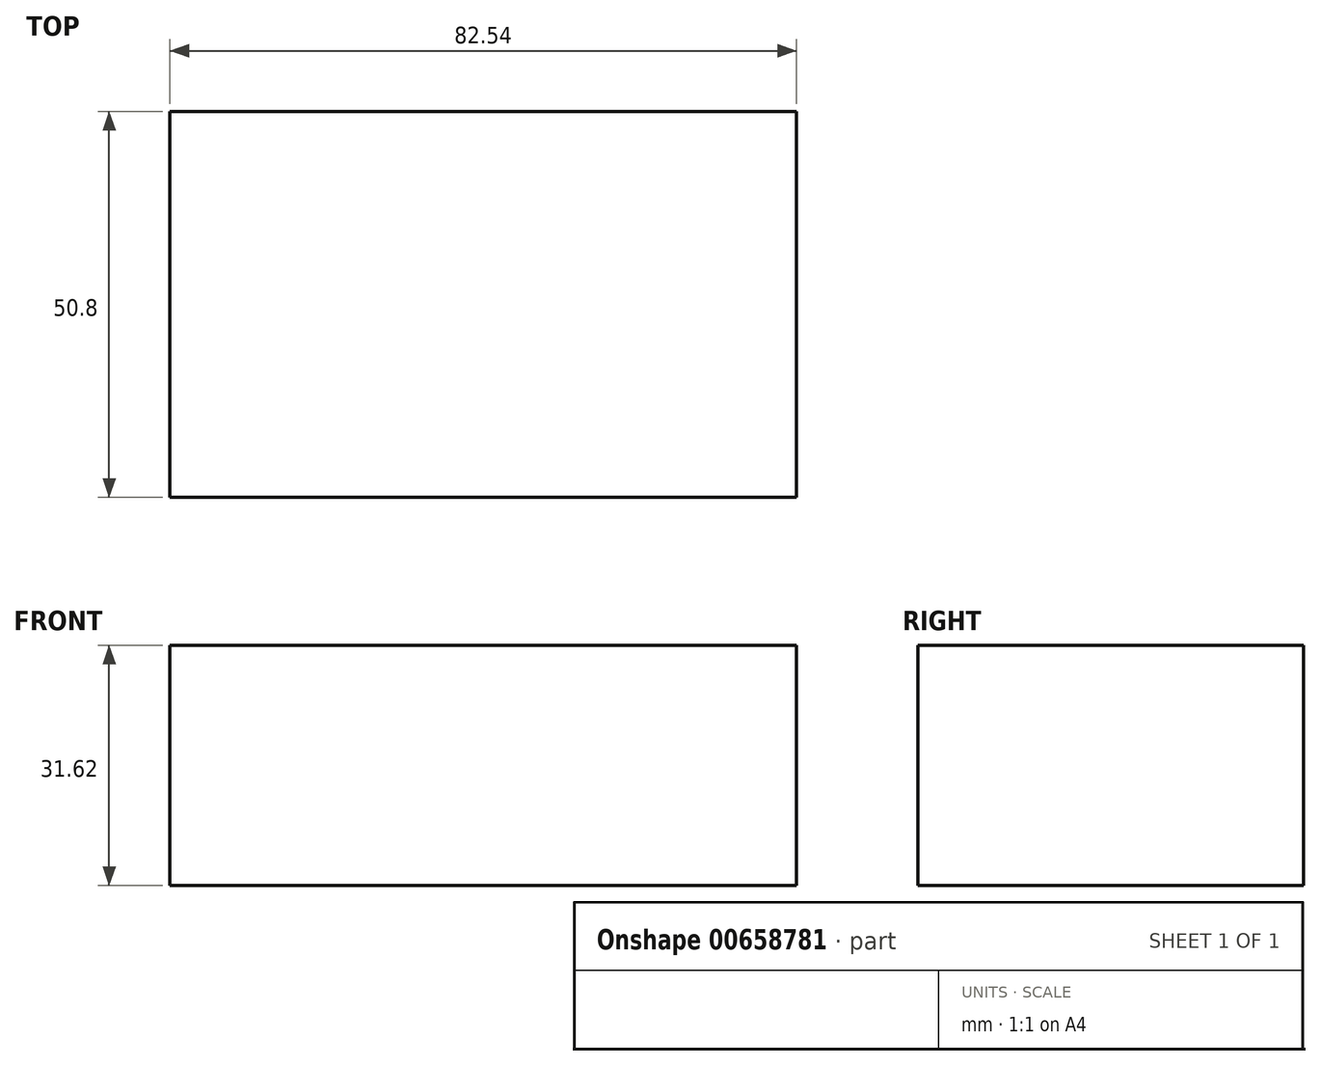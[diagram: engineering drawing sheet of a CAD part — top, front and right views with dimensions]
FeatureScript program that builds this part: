
annotation { "Feature Type Name" : "Feature", "Feature Type Description" : "" }
export const myFeature = defineFeature(function(context is Context, id is Id, definition is map)
    precondition{}
    {
        {
            var Q0;
            Q0=qCreatedBy(makeId("Front.planeOp"),FACE);
            var sketch = newSketch(context, id + "F0", { "sketchPlane" : qUnion([Q0])});
            skLineSegment(sketch, "E0.bottom", {"start": v(-41.27, 15.81) * mm, "end": v(41.27, 15.81) * mm});
            skLineSegment(sketch, "E0.top", {"start": v(-41.27, -15.81) * mm, "end": v(41.27, -15.81) * mm});
            skLineSegment(sketch, "E0.left", {"start": v(-41.28, 15.81) * mm, "end": v(-41.28, -15.81) * mm});
            skLineSegment(sketch, "E0.right", {"start": v(41.28, 15.81) * mm, "end": v(41.28, -15.81) * mm});
            skPoint(sketch, "E0.middle", {"position": v(0, 0) * mm});
            skLineSegment(sketch, "E1.bottom", {"start": v(64.61, 55.8) * mm, "end": v(95.33, 55.8) * mm});
            skLineSegment(sketch, "E1.top", {"start": v(64.61, 28.1) * mm, "end": v(95.33, 28.1) * mm});
            skLineSegment(sketch, "E1.left", {"start": v(64.61, 55.8) * mm, "end": v(64.61, 28.1) * mm});
            skLineSegment(sketch, "E1.right", {"start": v(95.33, 55.8) * mm, "end": v(95.33, 28.1) * mm});
            skPoint(sketch, "E1.middle", {"position": v(79.97, 41.96) * mm});
            skLineSegment(sketch, "E2", {"start": v(41.28, 15.81) * mm, "end": v(41.28, 26.3) * mm});
            skArc(sketch, "E3", {"start": v(41.28, 26.3) * mm, "mid": v(44.42, 33.04) * mm, "end": v(51.6, 34.97) * mm});
            skLineSegment(sketch, "E4", {"start": v(51.6, 34.97) * mm, "end": v(75.1, 34.97) * mm});
            skLineSegment(sketch, "E5.0", {"start": v(52.6, 50.21) * mm, "end": v(75.1, 50.21) * mm});
            skArc(sketch, "E5.1", {"start": v(26.03, 26.3) * mm, "mid": v(34, 44.17) * mm, "end": v(52.6, 50.21) * mm});
            skLineSegment(sketch, "E5.2", {"start": v(26.03, 15.81) * mm, "end": v(26.03, 26.3) * mm});
            skSolve(sketch);
        }
        {
            var Q0;
            Q0=makeQuery(id+"F0.imprint","IMPRINT",FACE,{"disambiguationData":[TD([[makeQuery(id+"F0.imprint","IMPRINT",EDGE,{"derivedFrom":sQuery(id+"F0.wireOp",EDGE,"E0.top")}),1.0]])]});
            extrude(context, id + "F1", {"entities" : qUnion([Q0]), "endBound" : BoundingType.SYMMETRIC, "depth" : 50.8 * mm, "offsetDistance" : 25.4 * mm, "hasDraft" : true, "draftAngle" : 0 * degree});
        }
    });
